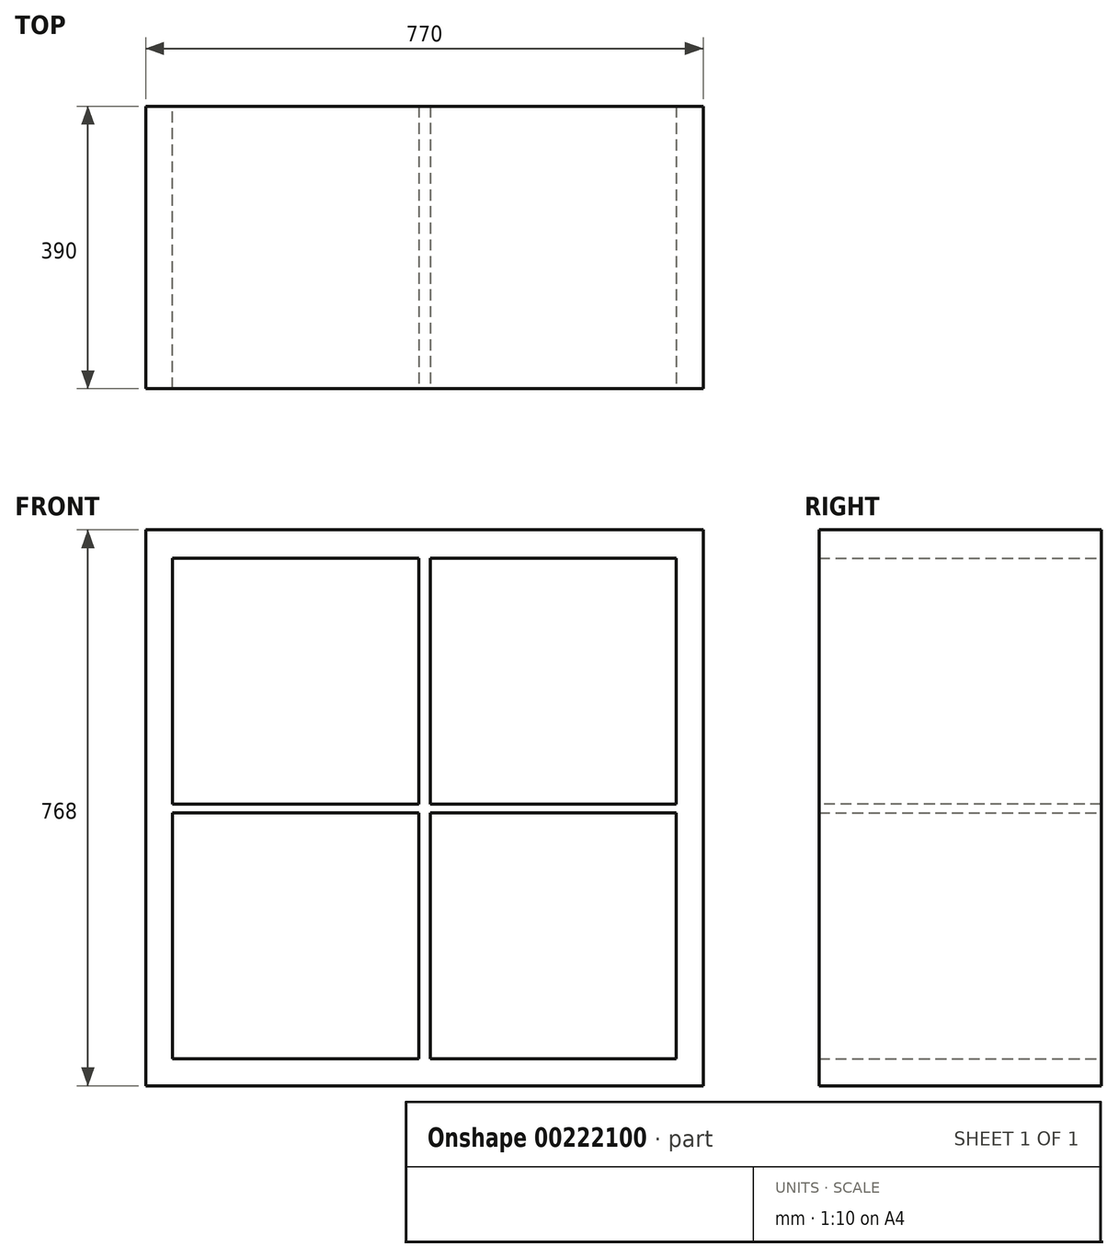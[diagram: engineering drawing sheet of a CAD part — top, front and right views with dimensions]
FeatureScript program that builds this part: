
annotation { "Feature Type Name" : "Feature", "Feature Type Description" : "" }
export const myFeature = defineFeature(function(context is Context, id is Id, definition is map)
    precondition{}
    {
        {
            var Q0;
            Q0=qCreatedBy(makeId("Top.planeOp"),FACE);
            var sketch = newSketch(context, id + "F0", { "sketchPlane" : qUnion([Q0])});
            skLineSegment(sketch, "E0.bottom", {"start": v(0, 0) * mm, "end": v(770, 0) * mm});
            skLineSegment(sketch, "E0.top", {"start": v(0, 390) * mm, "end": v(770, 390) * mm});
            skLineSegment(sketch, "E0.left", {"start": v(0, 0) * mm, "end": v(0, 390) * mm});
            skLineSegment(sketch, "E0.right", {"start": v(770, 0) * mm, "end": v(770, 390) * mm});
            skSolve(sketch);
        }
        {
            var Q0;
            Q0 = qSketchRegion(id + "F0", true);
            extrude(context, id + "F1", {"entities" : qUnion([Q0]), "depth" : 37 * mm});
        }
        {
            var Q0;
            Q0=makeQuery(id+"F1.opExtrude","CAP_FACE",FACE,{"disambiguationData":[OSD([sQuery(id+"F0.wireOp",EDGE,"E0.bottom"),sQuery(id+"F0.wireOp",EDGE,"E0.top"),sQuery(id+"F0.wireOp",EDGE,"E0.left"),sQuery(id+"F0.wireOp",EDGE,"E0.right")])],"isStart":false});
            var sketch = newSketch(context, id + "F2", { "sketchPlane" : qUnion([Q0])});
            skLineSegment(sketch, "E1.bottom", {"start": v(0, 0) * mm, "end": v(37, 0) * mm});
            skLineSegment(sketch, "E1.top", {"start": v(0, 390) * mm, "end": v(37, 390) * mm});
            skLineSegment(sketch, "E1.left", {"start": v(0, 0) * mm, "end": v(0, 390) * mm});
            skLineSegment(sketch, "E1.right", {"start": v(37, 0) * mm, "end": v(37, 390) * mm});
            skLineSegment(sketch, "E2.bottom", {"start": v(770, 0) * mm, "end": v(733, 0) * mm});
            skLineSegment(sketch, "E2.top", {"start": v(770, 390) * mm, "end": v(733, 390) * mm});
            skLineSegment(sketch, "E2.left", {"start": v(770, 0) * mm, "end": v(770, 390) * mm});
            skLineSegment(sketch, "E2.right", {"start": v(733, 0) * mm, "end": v(733, 390) * mm});
            skLineSegment(sketch, "E3.bottom", {"start": v(377, 390) * mm, "end": v(393, 390) * mm});
            skLineSegment(sketch, "E3.top", {"start": v(377, 0) * mm, "end": v(393, 0) * mm});
            skLineSegment(sketch, "E3.left", {"start": v(377, 390) * mm, "end": v(377, 0) * mm});
            skLineSegment(sketch, "E3.right", {"start": v(393, 390) * mm, "end": v(393, 0) * mm});
            skSolve(sketch);
        }
        {
            var Q0;
            Q0 = qSketchRegion(id + "F2", true);
            extrude(context, id + "F3", {"entities" : qUnion([Q0]), "operationType" : NewBodyOperationType.ADD, "depth" : 692 * mm});
        }
        {
            var Q0;
            Q0=makeQuery(id+"F3.opExtrude","CAP_FACE",FACE,{"disambiguationData":[OSD([sQuery(id+"F2.wireOp",EDGE,"E1.bottom"),sQuery(id+"F2.wireOp",EDGE,"E1.top"),sQuery(id+"F2.wireOp",EDGE,"E1.left"),sQuery(id+"F2.wireOp",EDGE,"E1.right")])],"isStart":false});
            var sketch = newSketch(context, id + "F4", { "sketchPlane" : qUnion([Q0])});
            skLineSegment(sketch, "E4.bottom", {"start": v(0, 390) * mm, "end": v(770, 390) * mm});
            skLineSegment(sketch, "E4.top", {"start": v(0, 0) * mm, "end": v(770, 0) * mm});
            skLineSegment(sketch, "E4.left", {"start": v(0, 390) * mm, "end": v(0, 0) * mm});
            skLineSegment(sketch, "E4.right", {"start": v(770, 390) * mm, "end": v(770, 0) * mm});
            skSolve(sketch);
        }
        {
            var Q0;
            Q0 = qSketchRegion(id + "F4", true);
            extrude(context, id + "F5", {"entities" : qUnion([Q0]), "operationType" : NewBodyOperationType.ADD, "depth" : 39 * mm});
        }
        {
            var Q0;
            Q0=makeQuery(id+"F3.opExtrude","SWEPT_FACE",FACE,{"disambiguationData":[OSD([sQuery(id+"F2.wireOp",EDGE,"E2.right")])]});
            var sketch = newSketch(context, id + "F6", { "sketchPlane" : qUnion([Q0])});
            skLineSegment(sketch, "E5.bottom", {"start": v(-390, 389) * mm, "end": v(0, 389) * mm});
            skLineSegment(sketch, "E5.top", {"start": v(-390, 377) * mm, "end": v(0, 377) * mm});
            skLineSegment(sketch, "E5.left", {"start": v(-390, 389) * mm, "end": v(-390, 377) * mm});
            skLineSegment(sketch, "E5.right", {"start": v(0, 389) * mm, "end": v(0, 377) * mm});
            skSolve(sketch);
        }
        {
            var Q0;
            Q0 = qSketchRegion(id + "F6", true);
            extrude(context, id + "F7", {"entities" : qUnion([Q0]), "operationType" : NewBodyOperationType.ADD, "depth" : 704 * mm});
        }
    });
